# Revit family: Lighting-Stradale-GEWISS-STREET[O3]-STAFFA_CORTA
name_source: partatom
category: Apparecchi per illuminazione
units: mm (PartAtom-declared; Revit-internal decimal feet)

## family parameters
Basato su piano di lavoro = Sì
Condiviso = No
Numero OmniClass = 23.80.00.00
Punto di calcolo locali = No
Quota connettore circolare = Usa diametro
Sempre verticale = Sì
Sorgente d'illuminazione = No
Taglio con vuoti quando caricato = No
Tipo di parte = Normale
Titolo OmniClass = Electric Power and Lighting

## types (1)
- GW87587 - Acciaio zincato - Grigio grafite - 0,5m
    Altezza da terra testa staffa = 272 mm
    Catalogo = LIGHTING
    Catalogo Serie = STREET [O3]
    Codice EAN = 8011564783065
    Codice Electrocod = 240
    Colore = Grigio grafite
    Descrizione = STREET STAFFA CORTA 0,5m GRIGIO GRAFITE
    Descrizione: = Staffa corta
    IDF = 5d71c9e0-c6fc-4576-9acd-83408b5b6280
    IDT = 3c9dcac4-61cc-486f-84a6-ab5b90133705
    Immagine tipo = GW87587.jpg
    L_staffa = 120 mm  [stored 0.393701 ft]
    Lunghezza = 0,5 m
    Materiale = Acciaio zincato
    Modello = GW87587
    Peso (kg) = 3,5
    Peso (kg): = 3,5
    Produttore = GEWISS S.p.A.
    Prospetto di default = 1219 mm
    SEO = Staffa
    Scheda Tecnica = https://www.gewiss.com
    Supporti = <Per categoria>
    Tubolare = <Per categoria>
    URL = https://www.gewiss.com
    Versione file RFA = 20.11

note: [stored X ft] marks values corroborated as IEEE doubles in the binary element streams (Revit-internal decimal feet)

## geometry (parser evidence)
native form markers: Blend x4
no freeform markers — native parametric forms only
